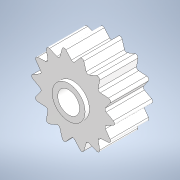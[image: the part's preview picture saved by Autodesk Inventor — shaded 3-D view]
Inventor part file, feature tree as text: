
AUTODESK INVENTOR PART (.ipt)
format: ipt  version: 2022.3 (Build 263350000, 350)  size: 376,320 bytes
history: native  units: mm
features: projected_geometry x5, extrude x2, sketch x2, imported_body x1
ambient origin geometry x8: Origin, YZ Plane, XZ Plane, XY Plane, X Axis, Y Axis, Z Axis, Center Point
bodies: Solid1 (feature_tree)
feature tree (10):
  extrude  "Extrusion1"  Depth=10.0mm TaperAngle=0.0deg
  extrude  "Extrusion2"  [1 undecoded]
  sketch  "Sketch1"  dims[d0=10.0mm d1=0.0mm d2=10.0mm d3=0.0mm]
  projected_geometry  "Projected Loop1"
  projected_geometry  "Projected Loop2"
  projected_geometry  "Projected Loop3"
  projected_geometry  "Projected Loop4"
  sketch  "Sketch2"
  projected_geometry  "Projected Loop5"
  imported_body  "Base1"
note: 1 required parameter value undecoded (feature->parameter linkage not recoverable at this tier; creation-order binding heuristic only, values carry confidence <= 0.55)
